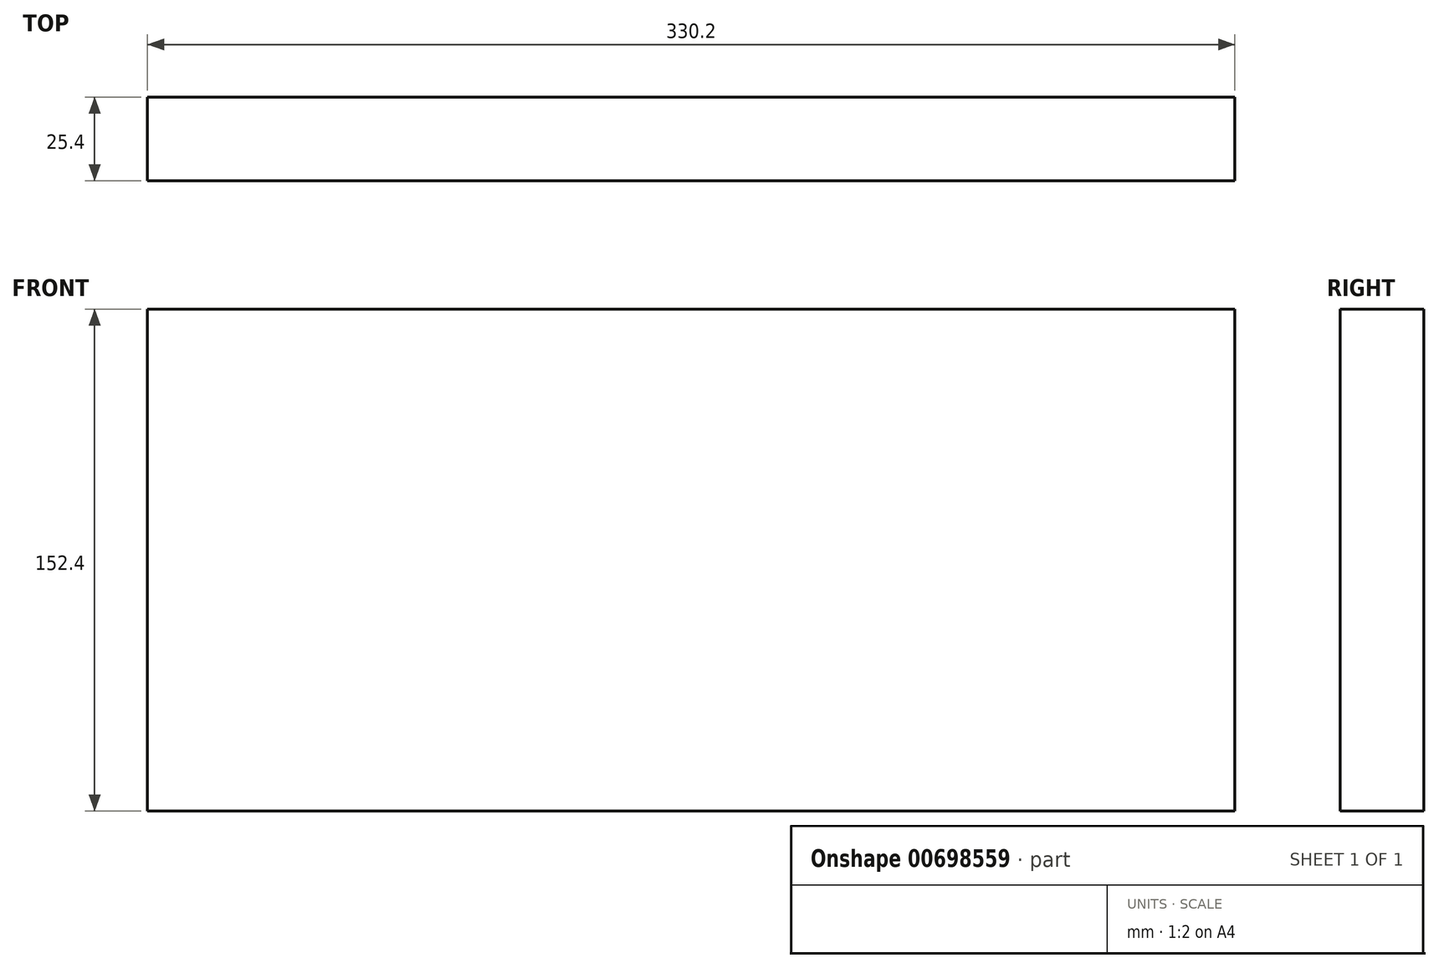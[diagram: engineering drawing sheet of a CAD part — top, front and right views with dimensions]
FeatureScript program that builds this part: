
annotation { "Feature Type Name" : "Feature", "Feature Type Description" : "" }
export const myFeature = defineFeature(function(context is Context, id is Id, definition is map)
    precondition{}
    {
        {
            var Q0;
            Q0=qCreatedBy(makeId("Front.planeOp"),FACE);
            var sketch = newSketch(context, id + "F0", { "sketchPlane" : qUnion([Q0])});
            skLineSegment(sketch, "E0.bottom", {"start": v(-278.89, 97.71) * mm, "end": v(51.31, 97.71) * mm});
            skLineSegment(sketch, "E0.top", {"start": v(-278.89, -54.69) * mm, "end": v(51.31, -54.69) * mm});
            skLineSegment(sketch, "E0.left", {"start": v(-278.89, 97.71) * mm, "end": v(-278.89, -54.69) * mm});
            skLineSegment(sketch, "E0.right", {"start": v(51.31, 97.71) * mm, "end": v(51.31, -54.69) * mm});
            skSolve(sketch);
        }
        {
            var Q0;
            Q0 = qSketchRegion(id + "F0", true);
            extrude(context, id + "F1", {"entities" : qUnion([Q0]), "depth" : 25.4 * mm, "offsetDistance" : 25.4 * mm});
        }
    });
